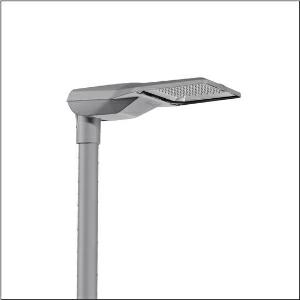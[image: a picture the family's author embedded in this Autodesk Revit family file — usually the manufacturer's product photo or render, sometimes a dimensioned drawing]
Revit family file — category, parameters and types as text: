
# Revit family: streetlight_sl_21_iq_midi___stw1_0a_5xe3e31g08mb_59a2
name_source: partatom
category: Lighting Fixtures
units: mm (PartAtom-declared; Revit-internal decimal feet)

## family parameters
Cut with Voids When Loaded = No
Host = Face
Light Source = No
Part Type = Normal
Room Calculation Point = No
Round Connector Dimension = Use Diameter
Shared = No

## types (1)
- --- (1 x LED, 19500 lm, 146.7 W, 3000K)
    Apparent Load = 147 VA
    CIE Flux Codes = 38 75 98 100 100
    Color Rendering = 70
    Color Temperature = 3000K
    Default Elevation = 1800 mm
    Description = Streetlight SL 21 iQ midi, mast luminaire, primary light control with lens, of PMMA, primary optical cover: cover, of toughened safety glass, transparent, light distribution: STW1.0a, light emission: direct distribution, primary light characteristic: asymmetric, installation type: post-top, side-entry, LED, High Power LED, rated luminous flux: 19.500lm, luminous efficacy: 133lm/W, light colour: 730, colour temperature: 3000K, control: Street-Remote, Auto-Match, Temp-Guard, Lumen-Switch, Night-Set, Smart-Wire, Light-Fading, Desk-Remote (wireless, voltage-free reading and setting of iQ features in the workshop via application-optimized NFC function/RFID function), optimised constant luminous flux control (CLO 2.0), pre-setting: linear dimming characteristic, mains connection: 230..240V, AC, 50/60Hz, start of lifetime: 147W, end of service life: 161W, reduction: 62W, luminaire housing, of diecast aluminium, powder-coated, Siteco® metallic grey (DB 702S), corrosivity category C5 mid according to DIN EN ISO 12944, please order mast flange separately, inclination adjustable: 0°, 5°, 10°, 15°, sealing non-destructively replaceable, multi-level sealing system, length: 644mm, width: 335mm, height: 110mm, mast flange for spigot size: 42mm (side-entry): 5XC10008XM4, 60/48mm (side-entry/post-top): 5XC10108XM2, 76/60mm (side-entry/post-top): 5XC10108XM1, protection rating (complete): IP66, insulation class (complete): insulation class II (safety insulation), certification: CE, ENEC, ENEC+, VDE, impact resistance: IK09, permissible operating ambient temperature for outdoor applications: -40..+50°C, standard-compliant lighting for roads and squares, packaging unit: 1 piece

Light Distribution: STW1.0a
    Height = 111 mm
    Lamp = 1 x LED
    Lamp Light Flux = 19500 lm
    Lamp Power = 146.7 W
    Lamp count = 1
    Length = 644 mm
    Luminous efficacy = 133 lm/W
    Manufacturer = Siteco
    ModVariant = No
    Model = 5XE3E31G08MB
    Number of Poles = 1
    OnlyDefault = Yes
    Power Factor = 1
    Product Name = Streetlight SL 21 iQ midi | STW1.0a
    Product group = mast luminaire | pylon top
    ProductGroupID = 6100
    Protection Class = Protection class II
    Protection Degree = IP 66
    RLX_Detail_Level = 1
    RLX_Emergency_Light_Flux = 0 lm
    RLX_Emergency_Type = 0
    RLX_Emergency_Type_DB = No
    RlxData = <blob elided: 90813 chars, md5=27fe38c1>
    Socket = socket
    Standby Power = 0 W
    System Light Flux = 19499 lm
    System Power = 147 W
    Type Comments = factory setting: luminous flux: 100 % | dim-lin: 254 | 753 mA
    Type Image = l_1004298.jpg
    URL = http://relux.com
    VarID = @adj_160213
    Voltage = 0 V
    Weight = 0.00 kg
    Width = 336 mm

## geometry (parser evidence)
native form markers: Blend x4, Sweep x11
no freeform markers — native parametric forms only
